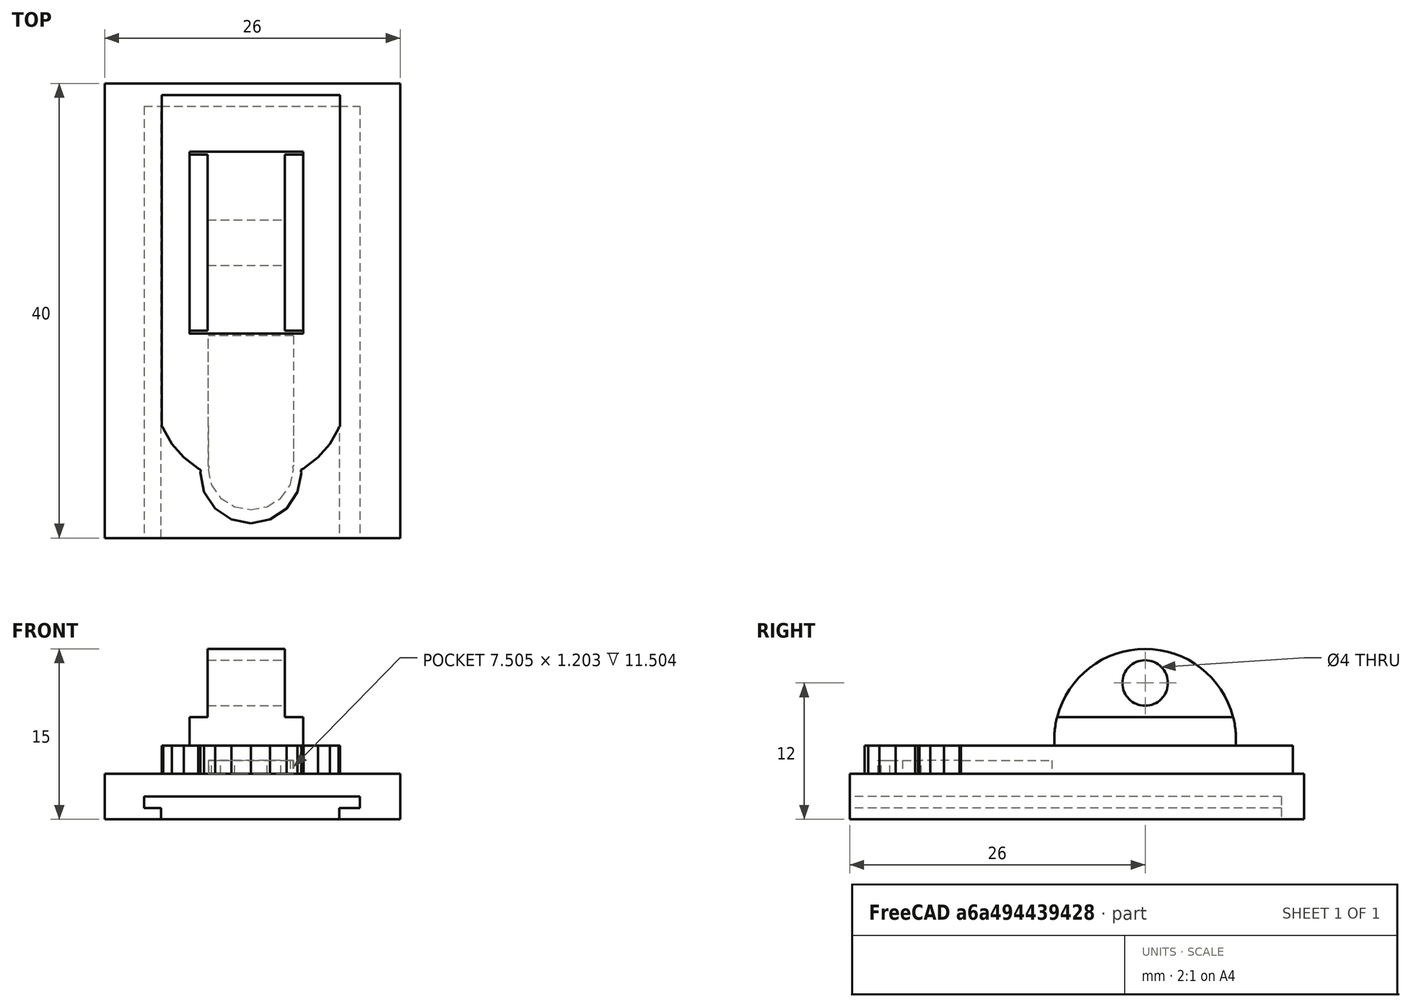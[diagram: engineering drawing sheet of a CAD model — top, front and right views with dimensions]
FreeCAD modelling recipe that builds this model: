
FCSTD DOCUMENT  (FreeCAD 0.18R13662 (Git))
Label: support
License: All rights reserved
LicenseURL: http://en.wikipedia.org/wiki/All_rights_reserved
objects: TechDraw::DrawViewDimension×20, Part::Cut×5, Part::Box×4, Part::MultiFuse×4, TechDraw::DrawProjGroupItem×3, Part::Cylinder×2, Part::Extrusion×2, Sketcher::SketchObject×1, Part::Part2DObjectPython×1, TechDraw::DrawSVGTemplate×1, TechDraw::DrawProjGroup×1, TechDraw::DrawPage×1
note: 19 computed .brp shape members not serialized (recipe doc carries the construction recipe); baked Part::Feature solids carry a one-line shape summary decoded from their .brp

FEATURE [Part::Box] Box002  label="Cubo002"
  AttacherType = Attacher::AttachEngine3D
  Height = 4
  Length = 22
  Placement = pos=(-1.5,-14,-33) rot=(0,0,1;0rad)
  Width = 40
FEATURE [Part::Box] Box003  label="Cubo003"
  AttacherType = Attacher::AttachEngine3D
  Height = 1
  Length = 19
  Placement = pos=(0,-14,0) rot=(0,0,1;0rad)
  Width = 39
FEATURE [Part::Box] Box004  label="Cubo004"
  AttacherType = Attacher::AttachEngine3D
  Height = 3.5
  Length = 15.7
  Placement = pos=(1.5,-14,0) rot=(0,0,1;0rad)
  Width = 39
FEATURE [Part::MultiFuse] Fusion001
  Placement = pos=(0,10,-31) rot=(1,0,0;3.14159rad)
  Shapes = -> [Box003,Box004]
FEATURE [Part::Cut] Cut004  label="base_finished001"
  Placement = pos=(21,62,-30) rot=(0,0,1;0rad)
FEATURE [Part::Cylinder] Cylinder003  label="Cilindro004"
  Angle = 360
  AttacherType = Attacher::AttachEngine3D
  Height = 10
  Placement = pos=(4,12,-26) rot=(0,1,0;1.5708rad)
  Radius = 8
FEATURE [Part::MultiFuse] Fusion002
  Shapes = -> [Cut004,Cylinder003]
FEATURE [Part::Cylinder] Cylinder004  label="Cilindro005"
  Angle = 360
  AttacherType = Attacher::AttachEngine3D
  Height = 10
  Placement = pos=(4,12,-21) rot=(0,1,0;1.5708rad)
  Radius = 2
FEATURE [Part::Cut] Cut005
  Base = -> Fusion002
  Tool = -> Cylinder004
FEATURE [Sketcher::SketchObject] Sketch
  Placement = pos=(0,0,0) rot=(1,0,0;1.5708rad)
  sketch-geometry (8):
    g0: LineSegment StartX=5.59956 StartY=-24 StartZ=0 EndX=3.74899 EndY=-24 EndZ=0
    g1: LineSegment StartX=3.74899 StartY=-24 StartZ=0 EndX=3.74899 EndY=-17.3582 EndZ=0
    g2: LineSegment StartX=3.74899 StartY=-17.3582 StartZ=0 EndX=5.59956 EndY=-17.3582 EndZ=0
    g3: LineSegment StartX=5.59956 StartY=-17.3582 StartZ=0 EndX=5.59956 EndY=-24 EndZ=0
    g4: LineSegment StartX=12.4021 StartY=-24 StartZ=0 EndX=14.8551 EndY=-24 EndZ=0
    g5: LineSegment StartX=14.8551 StartY=-24 StartZ=0 EndX=14.8551 EndY=-16.6637 EndZ=0
    g6: LineSegment StartX=14.8551 StartY=-16.6637 StartZ=0 EndX=12.4021 EndY=-16.6637 EndZ=0
    g7: LineSegment StartX=12.4021 StartY=-16.6637 StartZ=0 EndX=12.4021 EndY=-24 EndZ=0
  constraints (18):
    c: Coincident(g0,g1)
    c: Coincident(g1,g2)
    c: Coincident(g2,g3)
    c: Coincident(g3,g0)
    c: Horizontal(g0)
    c: Horizontal(g2)
    c: Vertical(g1)
    c: Vertical(g3)
    c: Coincident(g4,g5)
    c: Coincident(g5,g6)
    c: Coincident(g6,g7)
    c: Coincident(g7,g4)
    c: Horizontal(g4)
    c: Horizontal(g6)
    c: Vertical(g5)
    c: Vertical(g7)
    c: DistanceY(g0,g-1) = 24
    c: DistanceY(g4,g-1) = 24
FEATURE [Part::Extrusion] Extrude
  Base = -> Sketch
  Dir = (0,-1,0)
  DirMode = 2
  FaceMakerClass = Part::FaceMakerBullseye
  LengthFwd = 100
  LengthRev = 0
  Solid = true
  Symmetric = true
FEATURE [Part::Cut] Cut006
  Base = -> Cut005
  Tool = -> Extrude
FEATURE [Part::Box] Box005  label="Cubo005"
  AttacherType = Attacher::AttachEngine3D
  Height = 10
  Length = 10
  Placement = pos=(4,4,-40) rot=(0,0,1;0rad)
  Width = 17
FEATURE [Part::Cut] Cut007
  Base = -> Cut006
  Tool = -> Box005
FEATURE [Part::Cut] Cut008
  Base = -> Box002
  Tool = -> Fusion001
FEATURE [Part::MultiFuse] Fusion003
  Shapes = -> [Cut007,Cut008]
FEATURE [Part::Part2DObjectPython] DWire  # Draft 2D object (typed FeaturePython)
  ChamferSize = 0
  Closed = true
  End = (1.5,-14,-33)
  FilletRadius = 0
  Length = 70.6
  MakeFace = true
  Points = (17) [(-1.5,-14,-33),(-3.45582,-14,-33),(-3.45582,-14,-29.0598),(-3.45582,-14,-29),(-1.5,-14,-29),(20.5,-14,-29),(22.5442,-14,-29),(22.5442,-14,-33),+9 more]
  Start = (-1.5,-14,-33)
  Subdivisions = 0
  Support = -> [Fusion003]
FEATURE [Part::Extrusion] Extrude001
  Base = -> DWire
  Dir = (0,1,0)
  DirMode = 0
  FaceMakerClass = Part::FaceMakerBullseye
  LengthFwd = 40
  LengthRev = 0
  Solid = true
  Symmetric = false
FEATURE [Part::MultiFuse] Fusion
  Shapes = -> [Fusion003,Extrude001]
FEATURE [TechDraw::DrawSVGTemplate] Template
  EditableTexts = Designed_by_Name=Armando Astudillo Olalla,Drawing_number=1,FC-Date=08/09/2018,FC-SC=3:1,FC-SH=AAO,FC-Title=Support_v2 Syma Cam,+2 more (map truncated)
  Height = 210
  Orientation = 1
  Width = 297
FEATURE [TechDraw::DrawProjGroupItem] ProjItem  label="Front"
  CoarseView = false
  Direction = (0,-1,0)
  Focus = 100
  HardHidden = false
  IsoCount = 0
  IsoHidden = true
  IsoVisible = false
  LockPosition = true
  Perspective = false
  Rotation = 0
  RotationVector = (1,0,0)
  ScaleType = 0
  SeamHidden = true
  SeamVisible = false
  SmoothHidden = true
  SmoothVisible = false
  Source = -> [Fusion]
  Type = 0
  X = 80
  Y = 150
FEATURE [TechDraw::DrawProjGroupItem] ProjItem001  label="Left"
  CoarseView = false
  Direction = (-1,0,0)
  Focus = 100
  HardHidden = false
  IsoCount = 0
  IsoHidden = false
  IsoVisible = false
  LockPosition = true
  Perspective = false
  Rotation = 0
  RotationVector = (0,1,0)
  Scale = 2
  ScaleType = 2
  SeamHidden = false
  SeamVisible = false
  SmoothHidden = false
  SmoothVisible = false
  Source = -> [Fusion]
  Type = 1
  X = 200
  Y = 150
FEATURE [TechDraw::DrawProjGroupItem] ProjItem002  label="Top"
  CoarseView = false
  Direction = (0,0,1)
  Focus = 100
  HardHidden = false
  IsoCount = 0
  IsoHidden = false
  IsoVisible = false
  LockPosition = true
  Perspective = false
  Rotation = 0
  RotationVector = (1,0,0)
  Scale = 2
  ScaleType = 2
  SeamHidden = false
  SeamVisible = false
  SmoothHidden = false
  SmoothVisible = false
  Source = -> [Fusion]
  Type = 4
  X = 80
  Y = 65
FEATURE [TechDraw::DrawProjGroup] ProjGroup
  Anchor = -> ProjItem
  AutoDistribute = true
  CubeDirs = (1) [(0,0,0)]
  CubeRotations = (1) [(0,0,0)]
  LockPosition = false
  ProjectionType = 0
  Rotation = 0
  Scale = 2
  ScaleType = 2
  Source = -> [Fusion]
  Views = -> [ProjItem,ProjItem001,ProjItem002]
  X = 148.5
  Y = 105
  spacingX = 15
  spacingY = 15
FEATURE [TechDraw::DrawViewDimension] Dimension
  Arbitrary = false
  FormatSpec = %.2f
  LockPosition = false
  MeasureType = 1
  References2D = -> [ProjItem001]
  Rotation = 0
  ScaleType = 0
  Type = 1
  X = 4.56018
  Y = -39.5216
FEATURE [TechDraw::DrawViewDimension] Dimension001
  Arbitrary = false
  FormatSpec = %.2f
  LockPosition = false
  MeasureType = 1
  References2D = -> [ProjItem001]
  Rotation = 0
  ScaleType = 0
  Type = 2
  X = -50.5421
  Y = -34.9614
FEATURE [TechDraw::DrawViewDimension] Dimension002
  Arbitrary = false
  FormatSpec = %.2f
  LockPosition = false
  MeasureType = 1
  References2D = -> [ProjItem001]
  Rotation = 0
  ScaleType = 0
  Type = 2
  X = -62.8961
  Y = -3.73858
FEATURE [TechDraw::DrawViewDimension] Dimension003
  Arbitrary = false
  FormatSpec = %.2f
  LockPosition = false
  MeasureType = 1
  References2D = -> [ProjItem001]
  Rotation = 0
  ScaleType = 0
  Type = 5
  X = 28.1493
  Y = 27.2696
FEATURE [TechDraw::DrawViewDimension] Dimension004
  Arbitrary = false
  FormatSpec = %.2f
  LockPosition = false
  MeasureType = 1
  References2D = -> [ProjItem001]
  Rotation = 0
  ScaleType = 0
  Type = 5
  X = 40.4646
  Y = 19.7925
FEATURE [TechDraw::DrawViewDimension] Dimension005
  Arbitrary = false
  FormatSpec = %.2f
  LockPosition = false
  MeasureType = 1
  References2D = -> [ProjItem001]
  Rotation = 0
  ScaleType = 0
  Type = 2
  X = 63.9957
  Y = 12.5352
FEATURE [TechDraw::DrawViewDimension] Dimension006
  Arbitrary = false
  FormatSpec = %.2f
  LockPosition = false
  MeasureType = 1
  References2D = -> [ProjItem]
  Rotation = 0
  ScaleType = 0
  Type = 1
  X = 4.21506
  Y = 30.605
FEATURE [TechDraw::DrawViewDimension] Dimension007
  Arbitrary = false
  FormatSpec = %.2f
  LockPosition = false
  MeasureType = 1
  References2D = -> [ProjItem]
  Rotation = 0
  ScaleType = 0
  Type = 0
  X = -44.7684
  Y = 14.8559
FEATURE [TechDraw::DrawViewDimension] Dimension008
  Arbitrary = false
  FormatSpec = %.2f
  LockPosition = false
  MeasureType = 1
  References2D = -> [ProjItem001]
  Rotation = 0
  ScaleType = 0
  Type = 0
  X = -50.5903
  Y = 18.871
FEATURE [TechDraw::DrawViewDimension] Dimension009
  Arbitrary = false
  FormatSpec = %.2f
  LockPosition = false
  MeasureType = 1
  References2D = -> [ProjItem002]
  Rotation = 0
  ScaleType = 0
  Type = 0
  X = 1.49543
  Y = 57.3542
FEATURE [TechDraw::DrawViewDimension] Dimension010
  Arbitrary = false
  FormatSpec = %.2f
  LockPosition = false
  MeasureType = 1
  References2D = -> [ProjItem002]
  Rotation = 0
  ScaleType = 0
  Type = 0
  X = 0.967632
  Y = 51.0646
FEATURE [TechDraw::DrawViewDimension] Dimension011
  Arbitrary = false
  FormatSpec = %.2f
  LockPosition = false
  MeasureType = 1
  References2D = -> [ProjItem002]
  Rotation = 0
  ScaleType = 0
  Type = 0
  X = -44.9949
  Y = 51.3285
FEATURE [TechDraw::DrawViewDimension] Dimension012
  Arbitrary = false
  FormatSpec = %.2f
  LockPosition = false
  MeasureType = 1
  References2D = -> [ProjItem002]
  Rotation = 0
  ScaleType = 0
  Type = 2
  X = 48.9843
  Y = 0.722719
FEATURE [TechDraw::DrawViewDimension] Dimension013
  Arbitrary = false
  FormatSpec = %.2f
  LockPosition = false
  MeasureType = 1
  References2D = -> [ProjItem002]
  Rotation = 0
  ScaleType = 0
  Type = 2
  X = 37.9427
  Y = 11.8446
FEATURE [TechDraw::DrawViewDimension] Dimension014
  Arbitrary = false
  FormatSpec = %.2f
  LockPosition = false
  MeasureType = 1
  References2D = -> [ProjItem002]
  Rotation = 0
  ScaleType = 0
  Type = 0
  X = -38.1071
  Y = 15.4645
FEATURE [TechDraw::DrawViewDimension] Dimension015
  Arbitrary = false
  FormatSpec = %.2f
  LockPosition = false
  MeasureType = 1
  References2D = -> [ProjItem002]
  Rotation = 0
  ScaleType = 0
  Type = 0
  X = 38.0015
  Y = 50.9326
FEATURE [TechDraw::DrawViewDimension] Dimension016
  Arbitrary = false
  FormatSpec = %.2f
  LockPosition = false
  MeasureType = 1
  References2D = -> [ProjItem]
  Rotation = 0
  ScaleType = 0
  Type = 0
  X = -44.7285
  Y = -21.0282
FEATURE [TechDraw::DrawViewDimension] Dimension017
  Arbitrary = false
  FormatSpec = %.2f
  LockPosition = false
  MeasureType = 1
  References2D = -> [ProjItem]
  Rotation = 0
  ScaleType = 0
  Type = 0
  X = 37.2891
  Y = -0.381799
FEATURE [TechDraw::DrawViewDimension] Dimension018
  Arbitrary = false
  FormatSpec = %.2f
  LockPosition = false
  MeasureType = 1
  References2D = -> [ProjItem]
  Rotation = 0
  ScaleType = 0
  Type = 0
  X = -28.2183
  Y = -19.5146
FEATURE [TechDraw::DrawViewDimension] Dimension019
  Arbitrary = false
  FormatSpec = %.2f
  LockPosition = false
  MeasureType = 1
  References2D = -> [ProjItem]
  Rotation = 0
  ScaleType = 0
  Type = 0
  X = 31.6189
  Y = -19.0717
FEATURE [TechDraw::DrawPage] Page
  KeepUpdated = true
  ProjectionType = 0
  Template = -> Template
  Views = -> [ProjGroup,Dimension,Dimension001,Dimension002,Dimension003,Dimension004,Dimension005,Dimension006,Dimension007,Dimension008,Dimension009,Dimension010,Dimension011,Dimension012,Dimension013,Dimension014,Dimension015,Dimension016,Dimension017,Dimension018,Dimension019]
